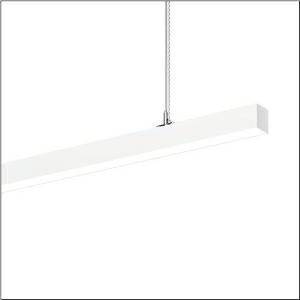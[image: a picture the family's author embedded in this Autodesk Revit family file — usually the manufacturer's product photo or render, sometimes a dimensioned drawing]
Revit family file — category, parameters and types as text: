
# Revit family: silica_21_51mx30tct9w
name_source: partatom
category: Lighting Fixtures
units: mm (PartAtom-declared; Revit-internal decimal feet)

## family parameters
Cut with Voids When Loaded = No
Host = Face
Light Source = No
Part Type = Normal
Room Calculation Point = No
Round Connector Dimension = Use Diameter
Shared = No

## types (1)
- --- (1 x LED, 10300 lm, 84.4 W, 6500K)
    Apparent Load = 84 VA
    CIE Flux Codes = 47 79 96 58 100
    Color Rendering = 80
    Color Temperature = 6500K
    Default Elevation = 1800 mm
    Description = Silica 21, office luminaire, primary optical cover: cover, of PMMA, opal, light emission: direct/indirect distribution, primary light characteristic: symmetric, installation type: suspended mounting, LED, rated luminous flux: 10.300lm, luminous efficacy: 116lm/W, light colour: 8tw, colour temperature: 2700..6500K, control gear: DALI DT8, with terminal, 3+2-pole, max. 2.5mm², mains connection: 220..240V, AC, 50/60Hz, rated input power: 88.7W, luminaire housing, of aluminium, traffic white (RAL 9016), length: 3.004mm, width: 53mm, height: 53mm, protection rating (complete): IP20, insulation class (complete): insulation class I (protective earthing), certification: CE, permissible operating ambient temperature: 0..+35°C, standard: EN 50419, packaging unit: 1 piece
    Height = 53 mm
    Lamp = 1 x LED
    Lamp Light Flux = 10300 lm
    Lamp Power = 84.4 W
    Lamp count = 1
    Length = 3004 mm
    Luminous efficacy = 122 lm/W
    Manufacturer = Siteco
    ModVariant = No
    Model = 51MX30TCT9W
    Mounting Place = Ceiling
    Mounting Type = Pendant
    Number of Poles = 1
    OnlyDefault = Yes
    Power Factor = 1
    Product Name = Silica 21
    Product group = office luminaire | ceiling pendant
    ProductGroupID = 903
    Protection Class = Protection class I
    Protection Degree = IP 20
    RLX_Detail_Level = 1
    RLX_Emergency_Light_Flux = 0 lm
    RLX_Emergency_Type = 0
    RLX_Emergency_Type_DB = No
    RlxData = <blob elided: 17517 chars, md5=2ad295b8>
    Socket = socket
    Standby Power = 0 W
    System Light Flux = 10300 lm
    System Power = 84 W
    Type Comments = individual setting
    Type Image = l_1349023.jpg
    URL = http://relux.com
    VarID = @adj_139139
    Voltage = 0 V
    Weight = 0.00 kg
    Width = 53 mm

## geometry (parser evidence)
native form markers: Blend x4, Sweep x14
no freeform markers — native parametric forms only
